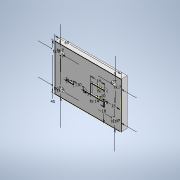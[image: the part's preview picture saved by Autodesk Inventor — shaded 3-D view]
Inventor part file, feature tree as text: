
AUTODESK INVENTOR PART (.ipt)
format: ipt  version: 2021 (Build 250183000, 183)  size: 237,568 bytes
history: native  units: in
note: dims shown in document units (in); Inventor stores cm internally (conversion verified against a paired STEP export)
features: other x7, extrude x4, sketch x3, hole x2, projected_geometry x2
ambient origin geometry x8: Origin, YZ Plane, XZ Plane, XY Plane, X Axis, Y Axis, Z Axis, Center Point
bodies: Solid1 (feature_tree)
feature tree (18):
  other  "points for corner holes and base plate"
  extrude  "Extrusion base plate"  Depth=2.5591in
  other  "plane above base plate to create rib"
  other  "channels and points for valves and for connectors"
  other  "channels as rib"
  extrude  "extrusion of rib to get cutout"  Depth=0.0394in
  sketch  "Sketch6"  dims[d26=1.7717in d27=2.5591in]
  extrude  "valve space extrusion"  Depth=0.2756in
  extrude  "valve bar extrusion"  Depth=0.0512in TaperAngle=0.0deg
  other  "Projected points for every valve"
  other  "all valve spaces"
  other  "projected point for connector holes"
  hole  "holes for connectors"  [1 undecoded]
  hole  "holes for corners"  [1 undecoded]
  sketch  "Sketch7"  dims[d28=0.2362in d29=0.0in d30=0.0394in]
  sketch  "Sketch11"  dims[d58=0.0984in d59=0.0689in d60=0.0512in d61=0.0in d62=0.0591in d63=0.1378in d66=0.0787in d67=0.0in d84=0.1614in d85=0.2362in d86=0.1575in d87=0.0787in d88=90.0deg d89=0.0512in d90=0.0in d91=0.2756in d92=0.2756in d93=0.2756in d94=0.2756in d95=0.2756in d96=0.2756in d97=0.2756in d98=0.2756in d99=0.1772in d100=0.2362in d101=0.1575in d102=0.0787in d103=90.0deg d104=0.315in d105=0.0in d106=0.3937in d107=0.5512in d108=0.5512in d109=0.2756in d110=0.3937in d111=0.2756in d116=0.5906in d117=0.7087in d126=0.0394in d127=0.0394in d128=0.0in d129=0.0in d130=0.0394in d131=0.0394in d132=0.2756in d133=0.2756in d134=0.0906in d135=0.0in d136=0.0295in d137=0.0689in d74=0.0197in d75=0.0344in d76=0.0197in d77=0.0344in]
  projected_geometry  "Projected Loop1"
  projected_geometry  "Projected Loop2"
note: 2 required parameter values undecoded (feature->parameter linkage not recoverable at this tier; creation-order binding heuristic only, values carry confidence <= 0.55)
